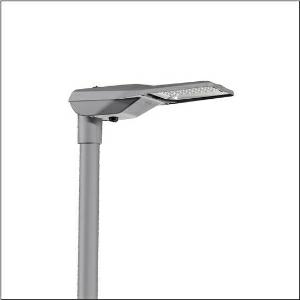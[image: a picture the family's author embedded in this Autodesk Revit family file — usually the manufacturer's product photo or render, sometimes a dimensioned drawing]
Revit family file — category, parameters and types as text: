
# Revit family: streetlight_sl_21_iq_mini___st1_0a_5xe2d61y08jb_b42a
name_source: partatom
category: Lighting Fixtures
units: mm (PartAtom-declared; Revit-internal decimal feet)

## family parameters
Cut with Voids When Loaded = No
Host = Face
Light Source = No
Part Type = Normal
Room Calculation Point = No
Round Connector Dimension = Use Diameter
Shared = No

## types (1)
- --- (1 x LED, 9730 lm, 72.5 W, 2700K)
    Apparent Load = 73 VA
    CIE Flux Codes = 40 73 97 100 100
    Color Rendering = 70
    Color Temperature = 2700K
    Default Elevation = 1800 mm
    Description = Streetlight SL 21 iQ mini, mast luminaire, primary light control with lens, of PMMA, primary optical cover: cover, of toughened safety glass, transparent, light distribution: ST1.0a, light emission: direct distribution, primary light characteristic: asymmetric, installation type: post-top, side-entry, LED, High Power LED, rated luminous flux: 9.730lm, luminous efficacy: 134lm/W, light colour: 727, colour temperature: 2700K, control gear: iQ-Street Remote, D4i with power reduction, control: pre-setting: logarithmic dimming characteristic, Street-Remote, Auto-Match, Temp-Guard, Lumen-Switch, Night-Set, Smart-Wire, Light-Fading, Desk-Remote (wireless, voltage-free reading and setting of iQ features in the workshop via application-optimized NFC function/RFID function), optimised constant luminous flux control (CLO 2.0), mains connection: 220..240V, AC, 50/60Hz, start of lifetime: 73W, end of service life: 76W, reduction: 33W, luminaire housing, of diecast aluminium, powder-coated, SITECO metallic grey (DB 702S), corrosivity category C5 high according to DIN EN ISO 12944, please order mast flange separately, inclination adjustable: 0°, 5°, 10°, 15°, sealing non-destructively replaceable, multi-level sealing system, length: 628mm, width: 235mm, height: 110mm, mast flange for spigot size: 42mm (side-entry): 5XC10008XM4, 60/48mm (side-entry/post-top): 5XC10108XM2, 76/60mm (side-entry/post-top): 5XC10108XM1, mounting height: 4..8m, Smart Interface below and above, protection rating (complete): IP66, insulation class (complete): insulation class II (safety insulation), certification: CE, ENEC, ENEC+, VDE, impact resistance: IK10, permissible operating ambient temperature for outdoor applications: -40..+50°C, standard-compliant lighting for roads and squares, packaging unit: 1 piece

Light Distribution: ST1.0a
    Height = 110 mm
    Lamp = 1 x LED
    Lamp Light Flux = 9730 lm
    Lamp Power = 72.5 W
    Lamp count = 1
    Length = 625 mm
    Luminous efficacy = 134 lm/W
    Manufacturer = Siteco
    ModVariant = No
    Model = 5XE2D61Y08JB
    Number of Poles = 1
    OnlyDefault = Yes
    Power Factor = 1
    Product Name = Streetlight SL 21 iQ mini | ST1.0a
    Product group = mast luminaire | pylon top
    ProductGroupID = 6100
    Protection Class = Protection class II
    Protection Degree = IP 66
    RLX_Detail_Level = 1
    RLX_Emergency_Light_Flux = 0 lm
    RLX_Emergency_Type = 0
    RLX_Emergency_Type_DB = No
    RlxData = <blob elided: 92405 chars, md5=7434288b>
    Socket = socket
    Standby Power = 0 W
    System Light Flux = 9730 lm
    System Power = 73 W
    Type Comments = factory setting: luminous flux: 100 % | dim-lin: 254 | 755 mA
    Type Image = l_1003514.jpg
    URL = http://relux.com
    VarID = @adj_114233
    Voltage = 0 V
    Weight = 0.00 kg
    Width = 234 mm

## geometry (parser evidence)
native form markers: Blend x4, Sweep x9
no freeform markers — native parametric forms only
